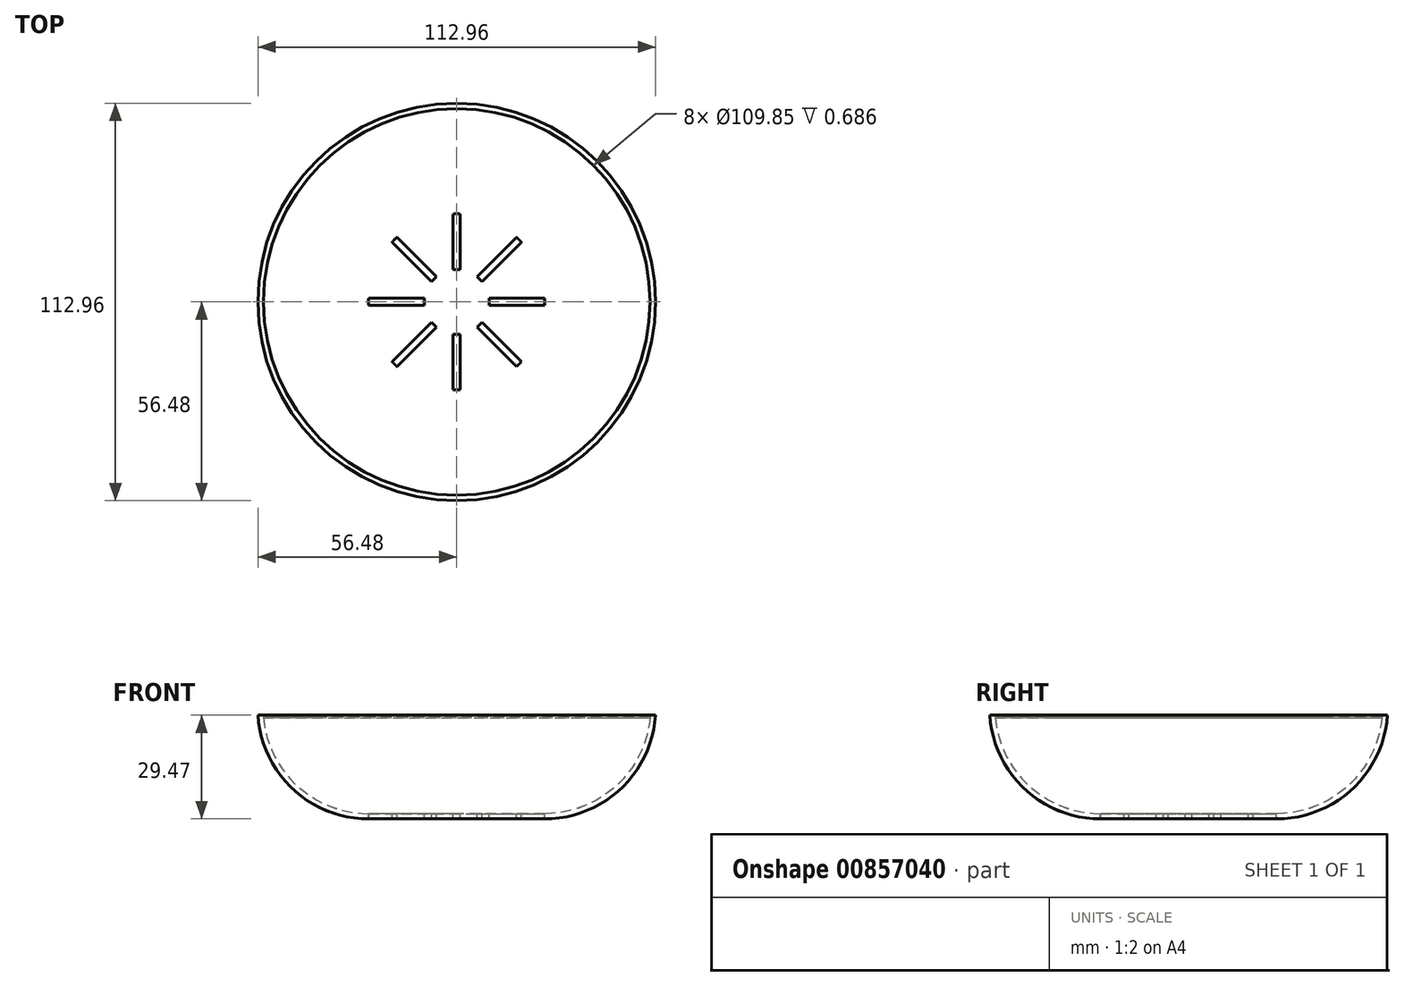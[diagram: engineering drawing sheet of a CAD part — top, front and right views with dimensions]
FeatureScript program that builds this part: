
annotation { "Feature Type Name" : "Feature", "Feature Type Description" : "" }
export const myFeature = defineFeature(function(context is Context, id is Id, definition is map)
    precondition{}
    {
        {
            var Q0;
            Q0=qCreatedBy(makeId("Front.planeOp"),FACE);
            var sketch = newSketch(context, id + "F0", { "sketchPlane" : qUnion([Q0])});
            skLineSegment(sketch, "E0", {"start": v(0, 0) * mm, "end": v(0, 88.86) * mm, "construction": true});
            skLineSegment(sketch, "E1", {"start": v(0, 0) * mm, "end": v(85.48, 0) * mm, "construction": true});
            skLineSegment(sketch, "E2", {"start": v(0, 0) * mm, "end": v(25, 0) * mm});
            skArc(sketch, "E3", {"start": v(25, 0) * mm, "mid": v(46.56, 8.52) * mm, "end": v(56.48, 29.47) * mm});
            skLineSegment(sketch, "E4", {"start": v(1.43, 1.5) * mm, "end": v(25, 1.5) * mm});
            skArc(sketch, "E5", {"start": v(25, 1.5) * mm, "mid": v(45.25, 9.34) * mm, "end": v(54.92, 28.78) * mm});
            skLineSegment(sketch, "E6", {"start": v(1.43, 1.5) * mm, "end": v(0, 1.5) * mm});
            skLineSegment(sketch, "E7", {"start": v(0, 1.5) * mm, "end": v(0, 0) * mm});
            skLineSegment(sketch, "E8", {"start": v(54.92, 28.78) * mm, "end": v(54.92, 29.47) * mm});
            skLineSegment(sketch, "E9", {"start": v(54.92, 29.47) * mm, "end": v(56.48, 29.47) * mm});
            skSolve(sketch);
        }
        {
            var Q0;
            Q0=makeQuery(id+"F0.imprint","IMPRINT",FACE,{"disambiguationData":[TD([[makeQuery(id+"F0.imprint","IMPRINT",EDGE,{"derivedFrom":sQuery(id+"F0.wireOp",EDGE,"E2")}),1.0]])]});
            var Q1;
            Q1=sQuery(id+"F0.wireOp",EDGE,"E0");
            revolve(context, id + "F1", {"surfaceOperationType" : NewSurfaceOperationType.NEW, "entities" : qUnion([Q0]), "axis" : qUnion([Q1]), "revolveType" : RevolveType.FULL});
        }
        {
            var Q0;
            Q0=makeQuery(id+"F1.opRevolve","SWEPT_FACE",FACE,{"disambiguationData":[OSD([sQuery(id+"F0.wireOp",EDGE,"E4"),sQuery(id+"F0.wireOp",EDGE,"E6")])]});
            var sketch = newSketch(context, id + "F2", { "sketchPlane" : qUnion([Q0])});
            skLineSegment(sketch, "E10", {"start": v(-9.2, 1) * mm, "end": v(-24.98, 1) * mm});
            skLineSegment(sketch, "E11", {"start": v(-9.2, 1) * mm, "end": v(-9.2, -1) * mm});
            skLineSegment(sketch, "E12", {"start": v(-9.2, -1) * mm, "end": v(-24.98, -1) * mm});
            skLineSegment(sketch, "E13", {"start": v(-9.2, 0) * mm, "end": v(-26.48, 0) * mm, "construction": true});
            skArc(sketch, "E14", {"start": v(-24.98, 1) * mm, "mid": v(-25.02, 0) * mm, "end": v(-24.98, -1) * mm});
            skSolve(sketch);
        }
        {
            var Q0;
            Q0 = qSketchRegion(id + "F2", true);
            extrude(context, id + "F3", {"entities" : qUnion([Q0]), "operationType" : NewBodyOperationType.REMOVE, "endBound" : BoundingType.THROUGH_ALL, "oppositeDirection" : true, "depth" : 25 * mm, "offsetDistance" : 25 * mm});
        }
        {
            var Q0;
            Q0=makeQuery(id+"F1.opRevolve","SWEPT_BODY",BODY,{"disambiguationData":[OSD([sQuery(id+"F0.wireOp",EDGE,"E2"),sQuery(id+"F0.wireOp",EDGE,"E3"),sQuery(id+"F0.wireOp",EDGE,"E4"),sQuery(id+"F0.wireOp",EDGE,"E5"),sQuery(id+"F0.wireOp",EDGE,"E6"),sQuery(id+"F0.wireOp",EDGE,"E7"),sQuery(id+"F0.wireOp",EDGE,"E8"),sQuery(id+"F0.wireOp",EDGE,"E9")])]});
            var Q1;
            Q1=sQuery(id+"F0.wireOp",EDGE,"E0");
            circularPattern(context, id + "F4", {"entities" : qUnion([Q0]), "axis" : qUnion([Q1]), "angle" : 360 * degree, "instanceCount" : 8, "equalSpace" : true});
        }
    });
